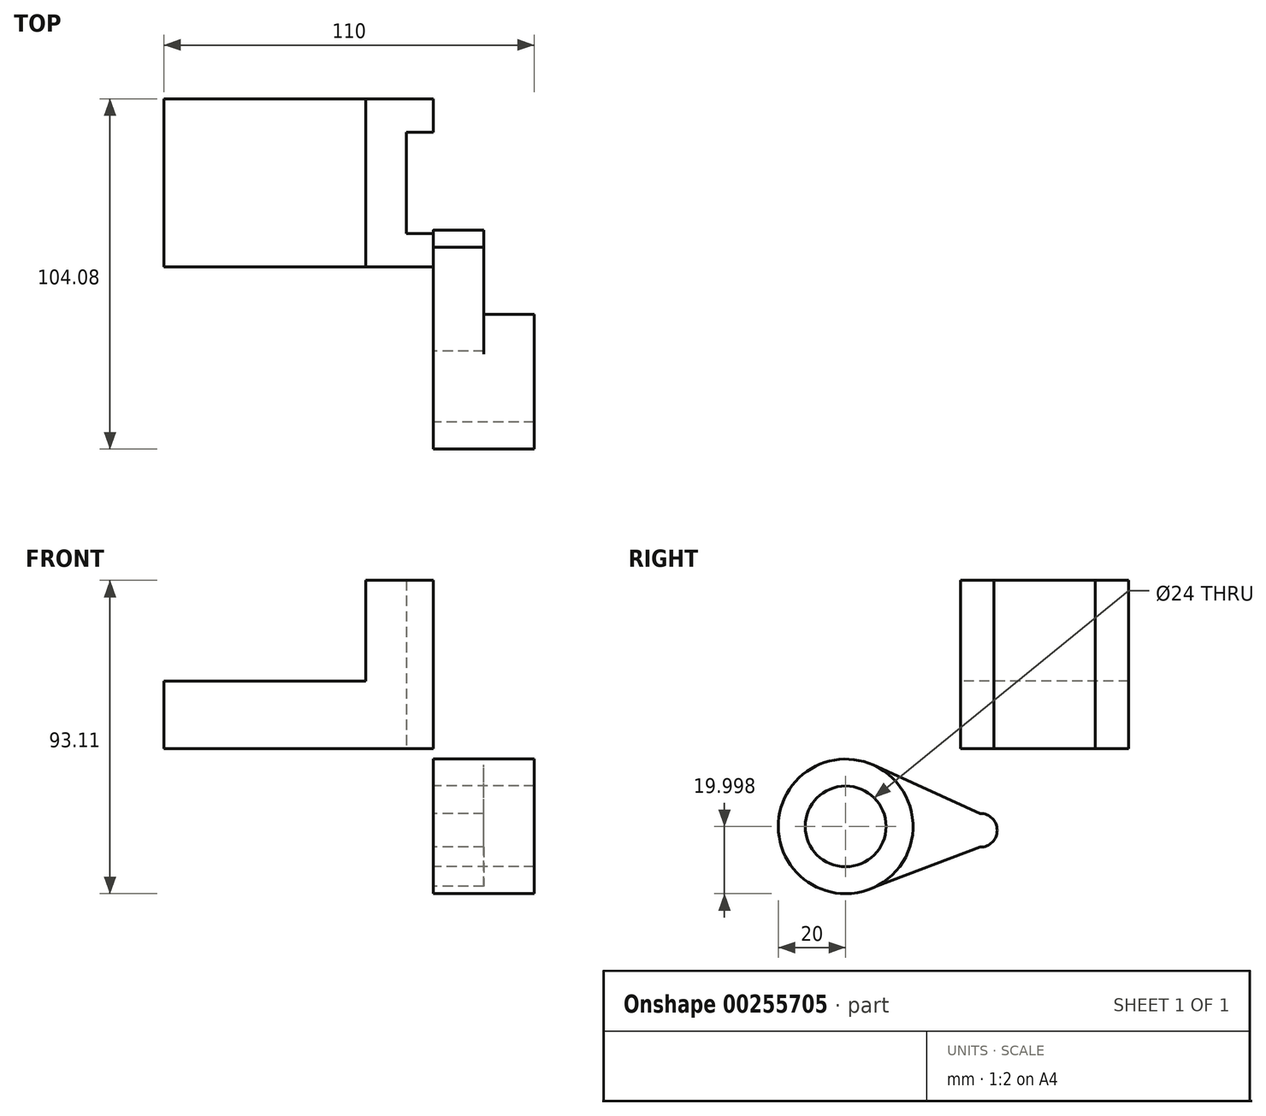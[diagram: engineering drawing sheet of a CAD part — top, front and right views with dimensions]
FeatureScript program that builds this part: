
annotation { "Feature Type Name" : "Feature", "Feature Type Description" : "" }
export const myFeature = defineFeature(function(context is Context, id is Id, definition is map)
    precondition{}
    {
        {
            var Q0;
            Q0=qCreatedBy(makeId("Top.planeOp"),FACE);
            var sketch = newSketch(context, id + "F0", { "sketchPlane" : qUnion([Q0])});
            skLineSegment(sketch, "E0", {"start": v(-80, 44.08) * mm, "end": v(-12.15, 44.08) * mm});
            skLineSegment(sketch, "E1.bottom", {"start": v(-80, 44.08) * mm, "end": v(0, 44.08) * mm});
            skLineSegment(sketch, "E1.top", {"start": v(-80, -5.92) * mm, "end": v(0, -5.92) * mm});
            skLineSegment(sketch, "E1.left", {"start": v(-80, 44.08) * mm, "end": v(-80, -5.92) * mm});
            skLineSegment(sketch, "E1.right", {"start": v(0, 44.08) * mm, "end": v(0, 34.08) * mm});
            skLineSegment(sketch, "E2", {"start": v(0, 34.08) * mm, "end": v(-8, 34.08) * mm});
            skLineSegment(sketch, "E3", {"start": v(0, 4.08) * mm, "end": v(-8, 4.08) * mm});
            skLineSegment(sketch, "E4.trimOffspring", {"start": v(0, 4.08) * mm, "end": v(0, -5.92) * mm});
            skLineSegment(sketch, "E5", {"start": v(-8, 34.08) * mm, "end": v(-8, 4.08) * mm});
            skLineSegment(sketch, "E6", {"start": v(-20, 44.08) * mm, "end": v(-20, -5.92) * mm});
            skPoint(sketch, "E7", {"position": v(-12.15, 44.08) * mm});
            skSolve(sketch);
        }
        {
            var Q0;
            {var subQ0=sQuery(id+"F0.wireOp",EDGE,"E1.left");Q0=makeQuery(id+"F0.imprint","IMPRINT",FACE,{"disambiguationData":[TD([[makeQuery(id+"F0.imprint","IMPRINT",EDGE,{"derivedFrom":subQ0}),1.0]])]});}
            extrude(context, id + "F1", {"entities" : qUnion([Q0]), "depth" : 20 * mm});
        }
        {
            var Q0;
            {var subQ0=sQuery(id+"F0.wireOp",EDGE,"E1.right");Q0=makeQuery(id+"F0.imprint","IMPRINT",FACE,{"disambiguationData":[TD([[makeQuery(id+"F0.imprint","IMPRINT",EDGE,{"derivedFrom":subQ0}),-1.0]])]});}
            extrude(context, id + "F2", {"entities" : qUnion([Q0]), "operationType" : NewBodyOperationType.ADD, "depth" : 50 * mm});
        }
        {
            var Q0;
            Q0=qCreatedBy(makeId("Right.planeOp"),FACE);
            var sketch = newSketch(context, id + "F3", { "sketchPlane" : qUnion([Q0])});
            skCircle(sketch, "E8", {"center": v(-40, -23.11) * mm, "radius": 20 * mm});
            skCircle(sketch, "E9", {"center": v(0, -24.27) * mm, "radius": 5 * mm});
            skCircle(sketch, "E10", {"center": v(-40, -23.11) * mm, "radius": 12 * mm});
            skLineSegment(sketch, "E11", {"start": v(0, -19.27) * mm, "end": v(-31.75, -4.9) * mm});
            skLineSegment(sketch, "E12", {"start": v(0, -29.27) * mm, "end": v(-30.94, -40.94) * mm});
            skSolve(sketch);
        }
        {
            var Q0;
            Q0=makeQuery(id+"F3.imprint","IMPRINT",FACE,{"disambiguationData":[TD([[makeQuery(id+"F3.imprint","IMPRINT",EDGE,{"derivedFrom":sQuery(id+"F3.wireOp",EDGE,"E10")}),-1.0]])]});
            extrude(context, id + "F4", {"entities" : qUnion([Q0]), "depth" : 30 * mm});
        }
        {
            var Q0;
            {var subQ0=sQuery(id+"F3.wireOp",EDGE,"E11");Q0=makeQuery(id+"F3.imprint","IMPRINT",FACE,{"disambiguationData":[TD([[makeQuery(id+"F3.imprint","IMPRINT",EDGE,{"derivedFrom":subQ0}),1.0]])]});}
            var Q1;
            {var subQ0=sQuery(id+"F3.wireOp",EDGE,"E9");var subQ1=makeQuery(id+"F3.imprint","INTERSECT",VERTEX,{"derivedFrom":[subQ0,sQuery(id+"F3.wireOp",EDGE,"E11")]});Q1=makeQuery(id+"F3.imprint","IMPRINT",FACE,{"disambiguationData":[TD([[makeQuery(id+"F3.imprint","IMPRINT",EDGE,{"disambiguationData":[TD([[subQ1,-1.0]])],"derivedFrom":subQ0}),1.0]])]});}
            extrude(context, id + "F5", {"entities" : qUnion([Q0, Q1]), "operationType" : NewBodyOperationType.ADD, "depth" : 15 * mm});
        }
    });
